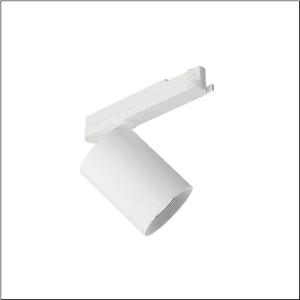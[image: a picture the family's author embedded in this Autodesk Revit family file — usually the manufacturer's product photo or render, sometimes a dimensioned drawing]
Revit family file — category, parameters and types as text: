
# Revit family: spot_21_51se13dbb5b
name_source: partatom
category: Lighting Fixtures
units: mm (PartAtom-declared; Revit-internal decimal feet)

## family parameters
Cut with Voids When Loaded = No
Host = Face
Light Source = No
Part Type = Normal
Room Calculation Point = No
Round Connector Dimension = Use Diameter
Shared = No

## types (1)
- --- (1 x LED, 5160 lm, 42.4 W, 3000K)
    Apparent Load = 42 VA
    CIE Flux Codes = 95 98 99 100 100
    Color Rendering = 90
    Color Temperature = 3000K
    Default Elevation = 1800 mm
    Description = Spot 21, directional spotlight, light control with lens, of PMMA, LED rated luminous flux: 5.120lm, light colour: 930, control gear: ECG Multilumen, with 3-phase adapter, mains connection: 220..240V, AC, 50/60Hz, of aluminium, traffic white (RAL 9016), length: 253mm, diameter: 105mm, protection rating (complete): IP20, insulation class (complete): insulation class I (protective earthing), certification: CE, impact resistance: IK02, permissible ambient temperature for indoor applications: -20..+40°C, packaging unit: 1 piece
    Height = 175 mm
    Lamp = 1 x LED
    Lamp Light Flux = 5160 lm
    Lamp Power = 42.4 W
    Lamp count = 1
    Length = 105 mm
    Luminous efficacy = 122 lm/W
    Manufacturer = Siteco
    ModVariant = No
    Model = 51SE13DBB5B
    Mounting Place = Ceiling
    Mounting Type = Pendant
    Number of Poles = 1
    OnlyDefault = Yes
    Power Factor = 1
    Product Name = Spot 21
    Product group = directional spotlight
    ProductGroupID = 905
    Protection Class = Protection class I
    Protection Degree = IP 20
    RLX_Detail_Level = 1
    RLX_Emergency_Light_Flux = 0 lm
    RLX_Emergency_Type = 0
    RLX_Emergency_Type_DB = No
    RlxData = <blob elided: 17673 chars, md5=0cea824b>
    Socket = socket
    Standby Power = 0 W
    System Light Flux = 5160 lm
    System Power = 42 W
    Type Comments = factory setting: luminous flux: 100 % | (ON | ON | ON | ON) | 1050 mA
    Type Image = l_1003976.jpg
    URL = http://relux.com
    VarID = @adj_075669
    Voltage = 0 V
    Weight = 0.00 kg
    Width = 0 mm  [stored 0 ft]

note: [stored X ft] marks values corroborated as IEEE doubles in the binary element streams (Revit-internal decimal feet)

## geometry (parser evidence)
native form markers: Blend x4, Sweep x11
no freeform markers — native parametric forms only
